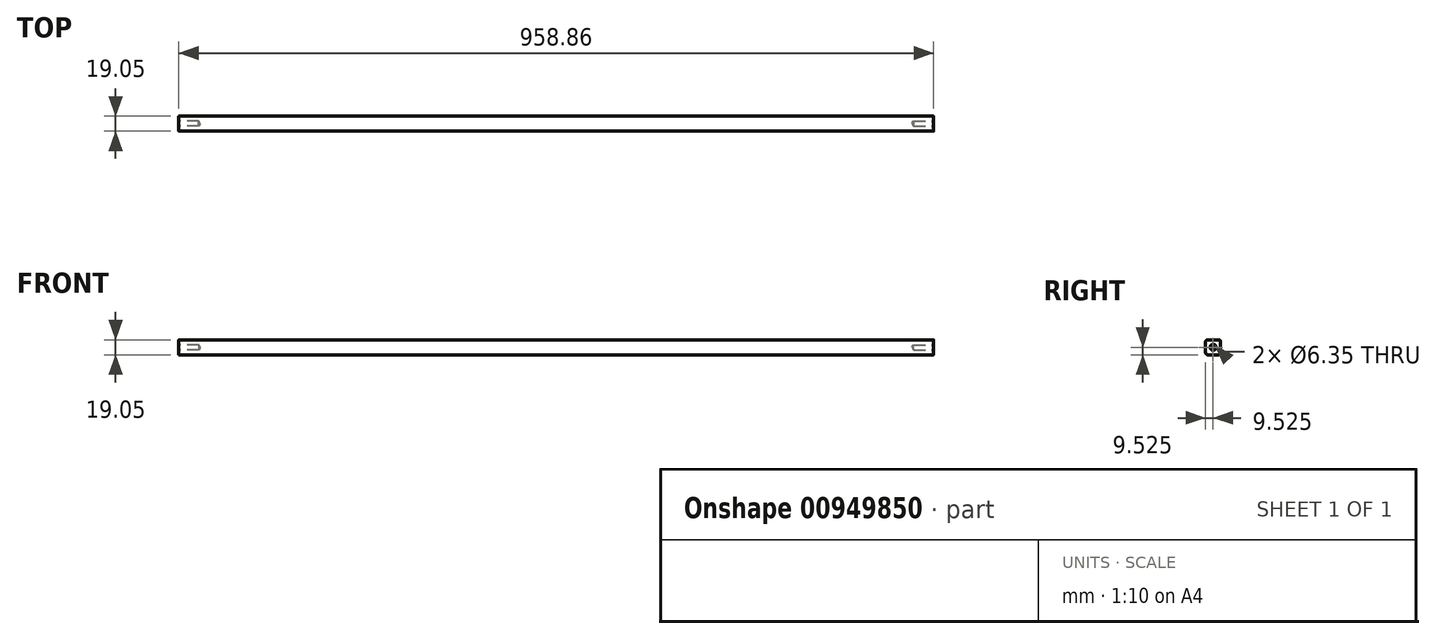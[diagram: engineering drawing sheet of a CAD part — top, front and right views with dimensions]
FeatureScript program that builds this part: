
annotation { "Feature Type Name" : "Feature", "Feature Type Description" : "" }
export const myFeature = defineFeature(function(context is Context, id is Id, definition is map)
    precondition{}
    {
        {
            var Q0;
            Q0=qCreatedBy(makeId("Right.planeOp"),FACE);
            var sketch = newSketch(context, id + "F0", { "sketchPlane" : qUnion([Q0])});
            skLineSegment(sketch, "E0.bottom", {"start": v(0, 0) * mm, "end": v(-19.05, 0) * mm});
            skLineSegment(sketch, "E0.top", {"start": v(0, 19.05) * mm, "end": v(-19.05, 19.05) * mm});
            skLineSegment(sketch, "E0.left", {"start": v(0, 0) * mm, "end": v(0, 19.05) * mm});
            skLineSegment(sketch, "E0.right", {"start": v(-19.05, 0) * mm, "end": v(-19.05, 19.05) * mm});
            skSolve(sketch);
        }
        {
            var Q0;
            Q0 = qSketchRegion(id + "F0", true);
            extrude(context, id + "F1", {"entities" : qUnion([Q0]), "endBound" : BoundingType.SYMMETRIC, "depth" : 958.85 * mm, "offsetDistance" : 25.4 * mm});
        }
        {
            var Q0;
            Q0=makeQuery(id+"F1.opExtrude","CAP_FACE",FACE,{"disambiguationData":[OSD([sQuery(id+"F0.wireOp",EDGE,"E0.bottom"),sQuery(id+"F0.wireOp",EDGE,"E0.top"),sQuery(id+"F0.wireOp",EDGE,"E0.left"),sQuery(id+"F0.wireOp",EDGE,"E0.right")])],"isStart":true});
            var sketch = newSketch(context, id + "F2", { "sketchPlane" : qUnion([Q0])});
            skLineSegment(sketch, "E1", {"start": v(0, 9.53) * mm, "end": v(19.05, 9.53) * mm, "construction": true});
            skPoint(sketch, "E2", {"position": v(9.53, 9.53) * mm});
            skSolve(sketch);
        }
        {
            var Q0;
            Q0=sQuery(id+"F2.wireOp",VERTEX,"E2");
            var Q1;
            Q1=makeQuery(id+"F1.opExtrude","SWEPT_BODY",BODY,{"disambiguationData":[OSD([sQuery(id+"F0.wireOp",EDGE,"E0.bottom"),sQuery(id+"F0.wireOp",EDGE,"E0.top"),sQuery(id+"F0.wireOp",EDGE,"E0.left"),sQuery(id+"F0.wireOp",EDGE,"E0.right")])]});
            hole(context, id + "F3", {"style" : HoleStyle.C_SINK, "endStyle" : HoleEndStyle.BLIND, "holeDiameter" : 6.35 * mm, "cSinkDiameter" : 7.62 * mm, "cSinkAngle" : 90 * degree, "majorDiameter" : 6.35 * mm, "holeDepth" : 25.4 * mm, "isTappedThrough" : true, "tappedDepth" : 12.7 * mm, "tapClearance" : 3, "startFromSketch" : true, "locations" : qUnion([Q0]), "scope" : qUnion([Q1])});
        }
        {
            var Q0;
            Q0=makeQuery(id+"F1.opExtrude","CAP_FACE",FACE,{"disambiguationData":[OSD([sQuery(id+"F0.wireOp",EDGE,"E0.bottom"),sQuery(id+"F0.wireOp",EDGE,"E0.top"),sQuery(id+"F0.wireOp",EDGE,"E0.left"),sQuery(id+"F0.wireOp",EDGE,"E0.right")])],"isStart":false});
            var sketch = newSketch(context, id + "F4", { "sketchPlane" : qUnion([Q0])});
            skLineSegment(sketch, "E3", {"start": v(-19.05, 9.53) * mm, "end": v(0, 9.53) * mm, "construction": true});
            skPoint(sketch, "E4", {"position": v(-9.53, 9.53) * mm});
            skSolve(sketch);
        }
        {
            var Q0;
            Q0=sQuery(id+"F4.wireOp",VERTEX,"E4");
            var Q1;
            Q1=makeQuery(id+"F1.opExtrude","SWEPT_BODY",BODY,{"disambiguationData":[OSD([sQuery(id+"F0.wireOp",EDGE,"E0.bottom"),sQuery(id+"F0.wireOp",EDGE,"E0.top"),sQuery(id+"F0.wireOp",EDGE,"E0.left"),sQuery(id+"F0.wireOp",EDGE,"E0.right")])]});
            hole(context, id + "F5", {"style" : HoleStyle.C_SINK, "endStyle" : HoleEndStyle.BLIND, "holeDiameter" : 6.35 * mm, "cSinkDiameter" : 7.62 * mm, "cSinkAngle" : 90 * degree, "majorDiameter" : 6.35 * mm, "holeDepth" : 25.4 * mm, "isTappedThrough" : true, "tappedDepth" : 12.7 * mm, "tapClearance" : 3, "startFromSketch" : true, "locations" : qUnion([Q0]), "scope" : qUnion([Q1])});
        }
        {
            var Q0;
            Q0=makeQuery(id+"F1.opExtrude","SWEPT_EDGE",EDGE,{"disambiguationData":[OSD([sQuery(id+"F0.wireOp",EDGE,"E0.top"),sQuery(id+"F0.wireOp",EDGE,"E0.right")])]});
            var Q1;
            Q1=makeQuery(id+"F1.opExtrude","SWEPT_EDGE",EDGE,{"disambiguationData":[OSD([sQuery(id+"F0.wireOp",EDGE,"E0.bottom"),sQuery(id+"F0.wireOp",EDGE,"E0.right")])]});
            var Q2;
            Q2=makeQuery(id+"F1.opExtrude","SWEPT_EDGE",EDGE,{"disambiguationData":[OSD([sQuery(id+"F0.wireOp",EDGE,"E0.bottom"),sQuery(id+"F0.wireOp",EDGE,"E0.left")])]});
            var Q3;
            Q3=makeQuery(id+"F1.opExtrude","SWEPT_EDGE",EDGE,{"disambiguationData":[OSD([sQuery(id+"F0.wireOp",EDGE,"E0.top"),sQuery(id+"F0.wireOp",EDGE,"E0.left")])]});
            fillet(context, id + "F6", {"entities" : qUnion([Q0, Q1, Q2, Q3]), "radius" : 2.54 * mm, "tangentPropagation" : true, "allowEdgeOverflow" : false});
        }
    });
